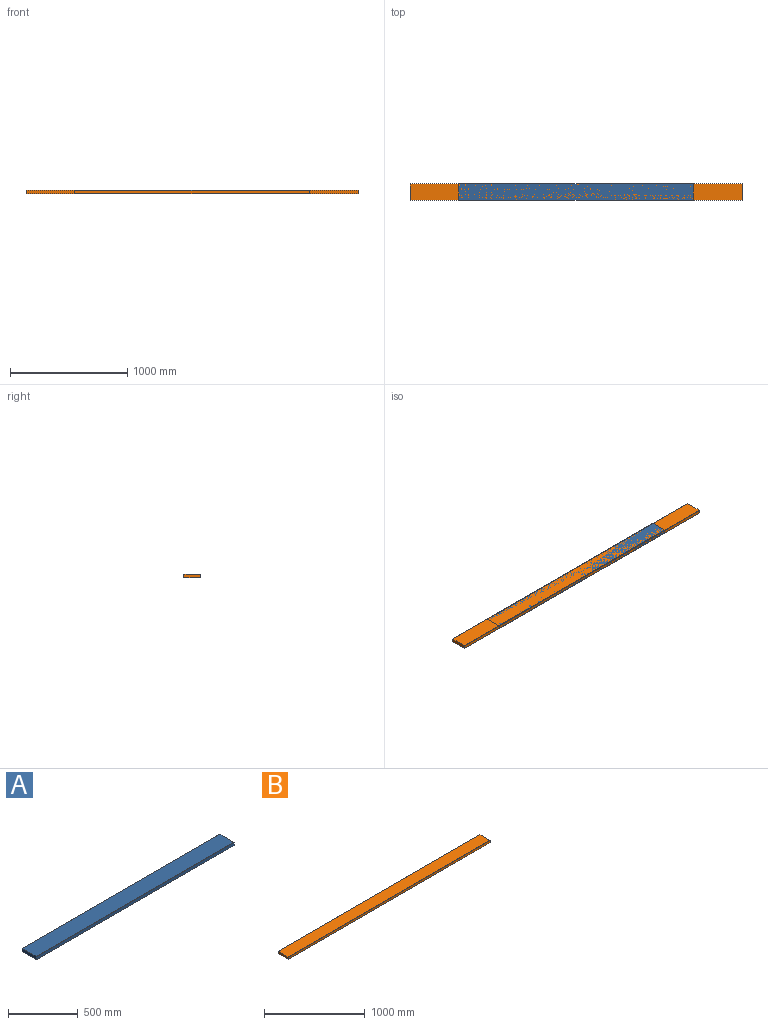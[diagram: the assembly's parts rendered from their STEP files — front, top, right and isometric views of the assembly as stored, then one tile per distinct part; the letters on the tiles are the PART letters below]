
ASSEMBLY  parts=2 mates=2
PART A: 8 faces, bbox 2000x145x28 mm
  f0: plane 2000x26mm, normal (0,1,0), area 52000mm2, adj f1,f3,f5,f7
  f1: plane 145x28mm, normal (-1,0,0), area 4058.3mm2, adj f0,f2,f4,f5,f6,f7
  f2: plane 2000x26mm, normal (0,-1,0), area 52000mm2, adj f1,f3,f5,f6
  f3: plane 145x28mm, normal (1,0,0), area 4058.3mm2, adj f0,f2,f4,f5,f6,f7
  f4: plane 2000x141mm, normal (0,0,1), area 282000mm2, adj f1,f3,f6,f7
  f5: plane 2000x145mm, normal (0,0,-1), area 290000mm2, adj f0,f1,f2,f3
  f6: cylinder r=2mm len=2000mm, axis (-1,0,0), area 6283.2mm2, adj f1,f2,f3,f4
  f7: cylinder r=2mm len=2000mm, axis (1,0,0), area 6283.2mm2, adj f0,f1,f3,f4
PART B: 8 faces, bbox 2833x143x28 mm
  f0: plane 2833x26mm, normal (0,1,0), area 73658mm2, adj f1,f3,f5,f7
  f1: plane 143x28mm, normal (-1,0,0), area 4002.3mm2, adj f0,f2,f4,f5,f6,f7
  f2: plane 2833x26mm, normal (0,-1,0), area 73658mm2, adj f1,f3,f5,f6
  f3: plane 143x28mm, normal (1,0,0), area 4002.3mm2, adj f0,f2,f4,f5,f6,f7
  f4: plane 2833x139mm, normal (0,0,1), area 393787mm2, adj f1,f3,f6,f7
  f5: plane 2833x143mm, normal (0,0,-1), area 405119mm2, adj f0,f1,f2,f3
  f6: cylinder r=2mm len=2833mm, axis (-1,0,0), area 8900.1mm2, adj f1,f2,f3,f4
  f7: cylinder r=2mm len=2833mm, axis (1,0,0), area 8900.1mm2, adj f0,f1,f3,f4
PLACE A t=(688.46,-298.45,4.26)mm
PLACE B t=(688.46,-299.45,4.26)mm
MATE planar B.f4 <-> A.f4  axis (0,0,1) through (-728.04,-229.95,32.26)mm
MATE planar A.f2 <-> B.f2  axis (0,-1,0) through (688.46,-370.95,17.26)mm
